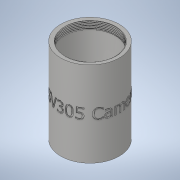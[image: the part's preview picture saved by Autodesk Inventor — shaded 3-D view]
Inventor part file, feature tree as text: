
AUTODESK INVENTOR PART (.ipt)
format: ipt  version: 2021.2 (Build 252289000, 289)  size: 1,206,784 bytes
history: native  units: in
note: dims shown in document units (in); Inventor stores cm internally (conversion verified against a paired STEP export)
features: sketch x4, extrude x3, plane x2, split x1, emboss x1
ambient origin geometry x8: Origin, YZ Plane, XZ Plane, XY Plane, X Axis, Y Axis, Z Axis, Center Point
bodies: Solid1 (feature_tree), Body1 (feature_tree)
feature tree (11):
  plane  "Work Plane1"
  split  "Split1"
  extrude  "Extrusion2"  Depth=3.5in TaperAngle=0.0deg
  extrude  "Extrusion3"  TaperAngle=0.0deg  [1 undecoded]
  extrude  "Extrusion4"  Depth=2.377in
  plane  "Work Plane2"
  emboss  "Emboss1"
  sketch  "Sketch2"  dims[d0=3.77in d3=3.5in d4=0.0in]
  sketch  "Sketch3"  dims[d5=0.25in d6=0.0in]
  sketch  "Sketch4"  dims[d7=1.4in d8=2.377in]
  sketch  "Sketch5"  dims[d9=2.0in d10=0.0in d11=2.0in d12=0.05in d13=0.0in]
note: 1 required parameter value undecoded (feature->parameter linkage not recoverable at this tier; creation-order binding heuristic only, values carry confidence <= 0.55)
